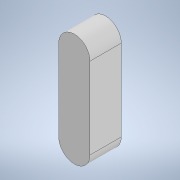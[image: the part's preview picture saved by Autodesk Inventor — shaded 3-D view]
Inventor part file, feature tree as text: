
AUTODESK INVENTOR PART (.ipt)
format: ipt  version: 2020 (Build 240168000, 168)  size: 94,208 bytes
history: native  units: mm
features: other x3, extrude x1, sketch x1, reference x1
ambient origin geometry x8: Origin, YZ Plane, XZ Plane, XY Plane, X Axis, Y Axis, Z Axis, Center Point
bodies: Body1 (feature_tree)
feature tree (6):
  other  "솔리드1"
  extrude  "돌출1"  Depth=5.0mm TaperAngle=0.0deg
  sketch  "스케치1"
  reference  "참조1"
  other  "조립품1"
  other  "Motor:1"
